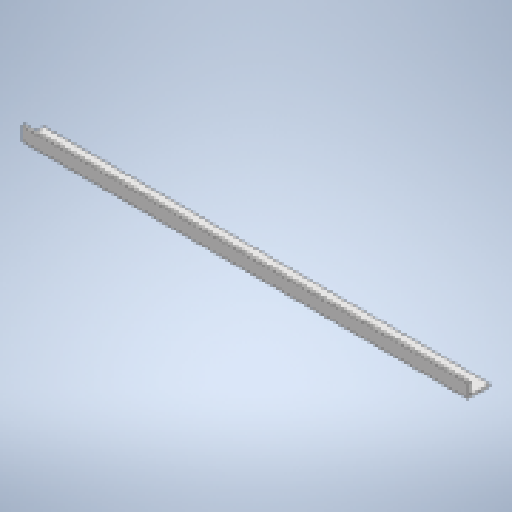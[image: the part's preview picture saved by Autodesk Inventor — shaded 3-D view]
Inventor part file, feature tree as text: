
AUTODESK INVENTOR PART (.ipt)
format: ipt  version: 2023 (Build 270158000, 158)  size: 139,776 bytes
history: native  units: in
note: dims shown in document units (in); Inventor stores cm internally (conversion verified against a paired STEP export)
features: extrude x1, sketch x1
ambient origin geometry x8: Origin, YZ Plane, XZ Plane, XY Plane, X Axis, Y Axis, Z Axis, Center Point
bodies: Solid1 (feature_tree)
feature tree (2):
  extrude  "Extrusion1"  Depth=2.3333in
  sketch  "Sketch1"  dims[d0=1.5in d1=2.3333in d2=0.25in d3=0.25in d4=48.0in d5=0.0in]
